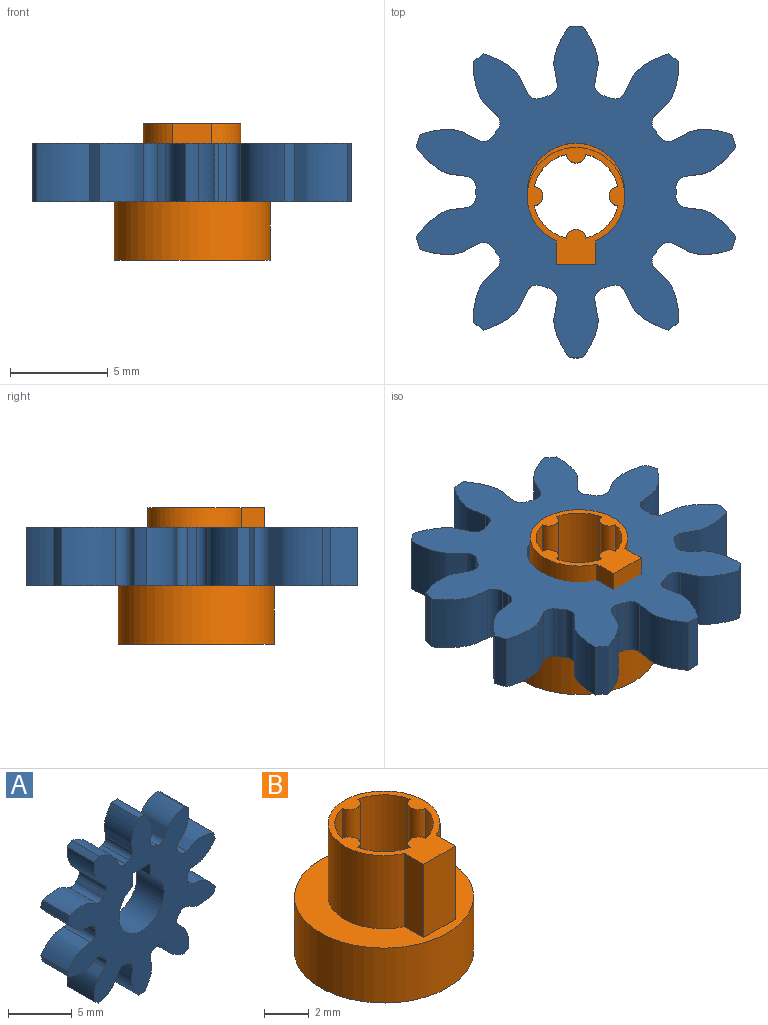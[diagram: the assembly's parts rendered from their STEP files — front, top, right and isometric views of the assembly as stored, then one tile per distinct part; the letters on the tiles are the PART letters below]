
ASSEMBLY  parts=2 mates=1
PART A: 66 faces, bbox 16.4x3x17.1 mm
  f0: cylinder r=8.5mm len=3mm, axis (0,1,0), area 2mm2, adj f9,f15,f56,f63
  f1: cylinder r=8.5mm len=3mm, axis (0,1,0), area 2mm2, adj f9,f15,f16,f58
  f2: cylinder r=8.5mm len=3mm, axis (0,1,0), area 2mm2, adj f9,f15,f46,f53
  f3: cylinder r=8.5mm len=3mm, axis (0,1,0), area 2mm2, adj f9,f15,f48,f61
  f4: cylinder r=8.5mm len=3mm, axis (0,1,0), area 2mm2, adj f9,f15,f36,f43
  f5: cylinder r=8.5mm len=3mm, axis (0,1,0), area 2mm2, adj f9,f15,f31,f38
  f6: cylinder r=8.5mm len=3mm, axis (0,1,0), area 2mm2, adj f9,f15,f26,f33
  f7: cylinder r=8.5mm len=3mm, axis (0,1,0), area 2mm2, adj f9,f15,f28,f51
  f8: cylinder r=8.5mm len=3mm, axis (0,1,0), area 2mm2, adj f9,f15,f23,f41
  f9: plane 17.05x16.43mm, normal (0,-1,0), area 124.3mm2, adj f0,f1,f2,f3,f4,f5,f6,f7
  f10: plane 3x1.21mm, normal (-1,0,0), area 3.6mm2, adj f9,f11,f13,f15
  f11: cylinder r=2.5mm len=5mm, axis (0,1,0), area 41mm2, adj f9,f10,f12,f15
  f12: plane 3x1.21mm, normal (1,0,0), area 3.6mm2, adj f9,f11,f13,f15
  f13: plane 3x2mm, normal (0,0,-1), area 6mm2, adj f9,f10,f12,f15
  f14: cylinder r=8.5mm len=3mm, axis (0,1,0), area 2mm2, adj f9,f15,f18,f21
  f15: plane 17.05x16.43mm, normal (0,1,0), area 124.3mm2, adj f0,f1,f2,f3,f4,f5,f6,f7
  f16: extruded ~3x2.58mm, area 9.3mm2, adj f1,f9,f15,f19
  f17: cylinder r=5.12mm len=3mm, axis (0,1,0), area 1.3mm2, adj f9,f15,f19,f20
  f18: extruded ~3x2.58mm, area 9.3mm2, adj f9,f14,f15,f20
  f19: cylinder r=0.56mm len=3mm, axis (0,1,0), area 2.5mm2, adj f9,f15,f16,f17
  f20: cylinder r=0.56mm len=3mm, axis (0,1,0), area 2.5mm2, adj f9,f15,f17,f18
  f21: extruded ~3x2.97mm, area 9.3mm2, adj f9,f14,f15,f24
  f22: cylinder r=5.12mm len=3mm, axis (0,1,0), area 1.3mm2, adj f9,f15,f24,f25
  f23: extruded ~3x2.73mm, area 9.3mm2, adj f8,f9,f15,f25
  f24: cylinder r=0.56mm len=3mm, axis (0,1,0), area 2.5mm2, adj f9,f15,f21,f22
  f25: cylinder r=0.56mm len=3mm, axis (0,1,0), area 2.5mm2, adj f9,f15,f22,f23
  f26: extruded ~3x2.58mm, area 9.3mm2, adj f6,f9,f15,f29
  f27: cylinder r=5.12mm len=3mm, axis (0,1,0), area 1.3mm2, adj f9,f15,f29,f30
  f28: extruded ~3x2.58mm, area 9.3mm2, adj f7,f9,f15,f30
  f29: cylinder r=0.56mm len=3mm, axis (0,1,0), area 2.5mm2, adj f9,f15,f26,f27
  f30: cylinder r=0.56mm len=3mm, axis (0,1,0), area 2.5mm2, adj f9,f15,f27,f28
  f31: extruded ~3x2.73mm, area 9.3mm2, adj f5,f9,f15,f34
  f32: cylinder r=5.12mm len=3mm, axis (0,1,0), area 1.3mm2, adj f9,f15,f34,f35
  f33: extruded ~3x2.97mm, area 9.3mm2, adj f6,f9,f15,f35
  f34: cylinder r=0.56mm len=3mm, axis (0,1,0), area 2.5mm2, adj f9,f15,f31,f32
  f35: cylinder r=0.56mm len=3mm, axis (0,1,0), area 2.5mm2, adj f9,f15,f32,f33
  f36: extruded ~3x2.92mm, area 9.3mm2, adj f4,f9,f15,f39
  f37: cylinder r=5.12mm len=3mm, axis (0,1,0), area 1.3mm2, adj f9,f15,f39,f40
  f38: extruded ~3x2.23mm, area 9.3mm2, adj f5,f9,f15,f40
  f39: cylinder r=0.56mm len=3mm, axis (0,1,0), area 2.5mm2, adj f9,f15,f36,f37
  f40: cylinder r=0.56mm len=3mm, axis (0,1,0), area 2.5mm2, adj f9,f15,f37,f38
  f41: extruded ~3x2.23mm, area 9.3mm2, adj f8,f9,f15,f44
  f42: cylinder r=5.12mm len=3mm, axis (0,1,0), area 1.3mm2, adj f9,f15,f44,f45
  f43: extruded ~3x2.92mm, area 9.3mm2, adj f4,f9,f15,f45
  f44: cylinder r=0.56mm len=3mm, axis (0,1,0), area 2.5mm2, adj f9,f15,f41,f42
  f45: cylinder r=0.56mm len=3mm, axis (0,1,0), area 2.5mm2, adj f9,f15,f42,f43
  f46: extruded ~3x2.23mm, area 9.3mm2, adj f2,f9,f15,f49
  f47: cylinder r=5.12mm len=3mm, axis (0,1,0), area 1.3mm2, adj f9,f15,f49,f50
  f48: extruded ~3x2.92mm, area 9.3mm2, adj f3,f9,f15,f50
  f49: cylinder r=0.56mm len=3mm, axis (0,1,0), area 2.5mm2, adj f9,f15,f46,f47
  f50: cylinder r=0.56mm len=3mm, axis (0,1,0), area 2.5mm2, adj f9,f15,f47,f48
  f51: extruded ~3x2.97mm, area 9.3mm2, adj f7,f9,f15,f54
  f52: cylinder r=5.12mm len=3mm, axis (0,1,0), area 1.3mm2, adj f9,f15,f54,f55
  f53: extruded ~3x2.73mm, area 9.3mm2, adj f2,f9,f15,f55
  f54: cylinder r=0.56mm len=3mm, axis (0,1,0), area 2.5mm2, adj f9,f15,f51,f52
  f55: cylinder r=0.56mm len=3mm, axis (0,1,0), area 2.5mm2, adj f9,f15,f52,f53
  f56: extruded ~3x2.73mm, area 9.3mm2, adj f0,f9,f15,f59
  f57: cylinder r=5.12mm len=3mm, axis (0,1,0), area 1.3mm2, adj f9,f15,f59,f60
  f58: extruded ~3x2.97mm, area 9.3mm2, adj f1,f9,f15,f60
  f59: cylinder r=0.56mm len=3mm, axis (0,1,0), area 2.5mm2, adj f9,f15,f56,f57
  f60: cylinder r=0.56mm len=3mm, axis (0,1,0), area 2.5mm2, adj f9,f15,f57,f58
  f61: extruded ~3x2.92mm, area 9.3mm2, adj f3,f9,f15,f64
  f62: cylinder r=5.12mm len=3mm, axis (0,1,0), area 1.3mm2, adj f9,f15,f64,f65
  f63: extruded ~3x2.23mm, area 9.3mm2, adj f0,f9,f15,f65
  f64: cylinder r=0.56mm len=3mm, axis (0,1,0), area 2.5mm2, adj f9,f15,f61,f62
  f65: cylinder r=0.56mm len=3mm, axis (0,1,0), area 2.5mm2, adj f9,f15,f62,f63
PART B: 18 faces, bbox 8x8x7 mm
  f0: cylinder r=2.2mm len=5mm, axis (0,0,-1), area 12.3mm2, adj f1,f7,f15,f17
  f1: cylinder r=0.5mm len=5mm, axis (0,0,-1), area 7.3mm2, adj f0,f2,f15,f17
  f2: cylinder r=2.2mm len=5mm, axis (0,0,-1), area 12.3mm2, adj f1,f3,f15,f17
  f3: cylinder r=0.5mm len=5mm, axis (0,0,-1), area 7.3mm2, adj f2,f4,f15,f17
  f4: cylinder r=2.2mm len=5mm, axis (0,0,-1), area 12.3mm2, adj f3,f5,f15,f17
  f5: cylinder r=0.5mm len=5mm, axis (0,0,-1), area 7.3mm2, adj f4,f6,f15,f17
  f6: cylinder r=2.2mm len=5mm, axis (0,0,-1), area 12.3mm2, adj f5,f7,f15,f17
  f7: cylinder r=0.5mm len=5mm, axis (0,0,-1), area 7.3mm2, adj f0,f6,f15,f17
  f8: cylinder r=4mm len=8mm, axis (0,0,-1), area 75.4mm2, adj f9,f10
  f9: plane 8x8mm, normal (0,0,1), area 28.5mm2, adj f8,f11,f12,f13,f14
  f10: plane 8x8mm, normal (0,0,-1), area 17.1mm2, adj f8,f16
  f11: cylinder r=2.5mm len=5mm, axis (0,0,-1), area 54.6mm2, adj f9,f12,f14,f15
  f12: plane 4x1.21mm, normal (-1,0,0), area 4.8mm2, adj f9,f11,f13,f15
  f13: plane 4x2mm, normal (0,-1,0), area 8mm2, adj f9,f12,f14,f15
  f14: plane 4x1.21mm, normal (1,0,0), area 4.8mm2, adj f9,f11,f13,f15
  f15: plane 6x5mm, normal (0,0,1), area 8.1mm2, adj f0,f1,f2,f3,f4,f5,f6,f7
  f16: cylinder r=3.25mm len=6.5mm, axis (0,0,1), area 40.8mm2, adj f10,f17
  f17: plane 6.5x6.5mm, normal (0,0,-1), area 19.5mm2, adj f0,f1,f2,f3,f4,f5,f6,f7
PLACE A rot(axis=(1,0,0),90deg) t=(0,0.22,15)mm
PLACE B t=(0,0,-5)mm
MATE fastened A.f0 <-> B.f9  axis (0,0,-1) through (0,0.22,12)mm
